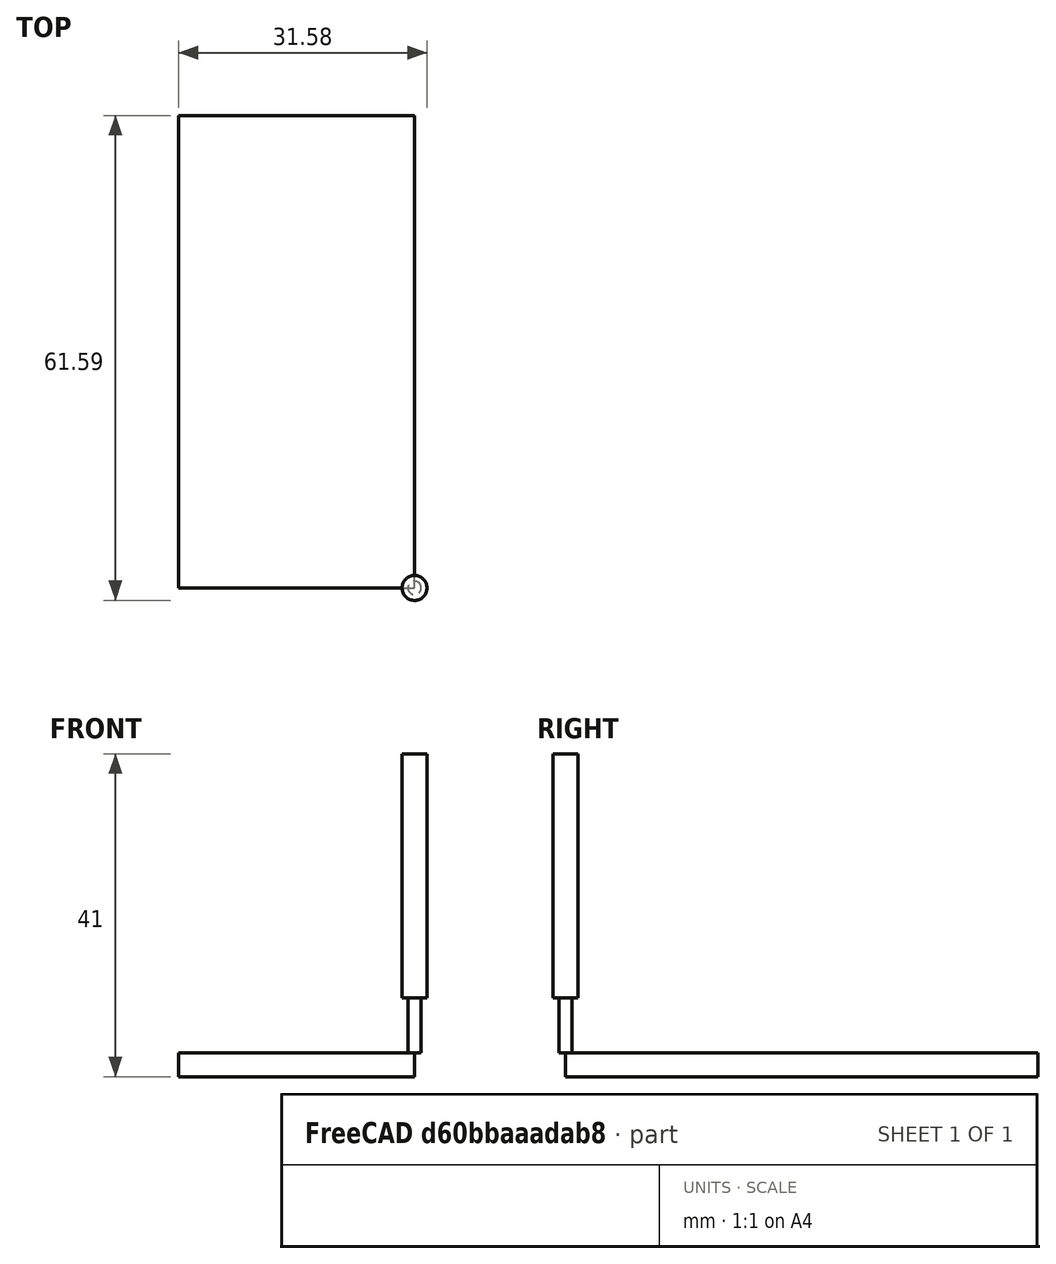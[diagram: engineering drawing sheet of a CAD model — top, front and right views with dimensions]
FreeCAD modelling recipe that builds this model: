
FCSTD DOCUMENT  (FreeCAD 0.20R29603 (Git))
Label: Кріплення дротів (CNC 3018 PLUS)
License: All rights reserved
LicenseURL: http://en.wikipedia.org/wiki/All_rights_reserved
objects: Path::FeaturePython×4, Part::FeaturePython×3, App::DocumentObjectGroup×3, Sketcher::SketchObject×1, PartDesign::Pad×1, PartDesign::Body×1, App::FeaturePython×1, Mesh::FeaturePython×1
note: 9 computed .brp shape members not serialized (recipe doc carries the construction recipe); baked Part::Feature solids carry a one-line shape summary decoded from their .brp

FEATURE [Sketcher::SketchObject] Sketch
  FullyConstrained = true
  MapMode = 5
  Support = -> [XY_Plane]
  sketch-geometry (10):
    g0: LineSegment StartX=-30 StartY=60 StartZ=0 EndX=0 EndY=60 EndZ=0
    g1: LineSegment StartX=0 StartY=60 StartZ=0 EndX=0 EndY=0 EndZ=0
    g2: LineSegment StartX=0 StartY=0 StartZ=0 EndX=-30 EndY=0 EndZ=0
    g3: LineSegment StartX=-30 StartY=0 StartZ=0 EndX=-30 EndY=60 EndZ=0
    g4: Circle CenterX=-22.5 CenterY=5 CenterZ=0 NormalX=0 NormalY=0 NormalZ=1 AngleXU=0 Radius=2.5
    g5: Circle CenterX=-7.5 CenterY=5 CenterZ=0 NormalX=0 NormalY=0 NormalZ=1 AngleXU=0 Radius=2.5
    g6: Circle CenterX=-25 CenterY=55 CenterZ=0 NormalX=0 NormalY=0 NormalZ=1 AngleXU=0 Radius=2
    g7: Circle CenterX=-5 CenterY=55 CenterZ=0 NormalX=0 NormalY=0 NormalZ=1 AngleXU=0 Radius=2
    g8: Circle CenterX=-25 CenterY=30 CenterZ=0 NormalX=0 NormalY=0 NormalZ=1 AngleXU=0 Radius=2
    g9: Circle CenterX=-5 CenterY=30 CenterZ=0 NormalX=0 NormalY=0 NormalZ=1 AngleXU=0 Radius=2
  constraints (29):
    c: Coincident(g0,g1)
    c: Coincident(g1,g2)
    c: Coincident(g2,g3)
    c: Coincident(g3,g0)
    c: Horizontal(g0)
    c: Horizontal(g2)
    c: Vertical(g1)
    c: Vertical(g3)
    c: Coincident(g1,g-1)
    c: DistanceY(g3,g3) = 60
    c: DistanceX(g0,g0) = 30
    c: Distance(g4,g2) = 5
    c: Distance(g5,g2) = 5
    c: Distance(g4,g5) = 15
    c: Diameter(g4) = 5
    c: Diameter(g5) = 5
    c: Distance(g4,g3) = 7.5
    c: Diameter(g6) = 4
    c: Diameter(g7) = 4
    c: Distance(g6,g0) = 5
    c: Distance(g7,g0) = 5
    c: Distance(g6,g3) = 5
    c: Distance(g7,g1) = 5
    c: Diameter(g9) = 4
    c: Diameter(g8) = 4
    c: Distance(g8,g3) = 5
    c: Distance(g9,g1) = 5
    c: Distance(g6,g8) = 25
    c: Distance(g7,g9) = 25
FEATURE [PartDesign::Pad] Pad
  Direction = (0,0,1)
  Length = 3
  Length2 = 10
  Profile = -> Sketch
  ReferenceAxis = -> Sketch [N_Axis]
  Reversed = true
  Type = 0
FEATURE [PartDesign::Body] Body
  Group = -> [Sketch,Pad]
  Origin = -> Origin
  Tip = -> Pad
FEATURE [App::FeaturePython] SetupSheet  # Path/CAM operation (typed FeaturePython)
  ClearanceHeightExpression = OpStockZMax+SetupSheet.ClearanceHeightOffset
  ClearanceHeightOffset = 5
  CoolantMode = 0
  CoolantModes = None | Flood | Mist
  FinalDepthExpression = OpFinalDepth
  HorizRapid = 0
  SafeHeightExpression = OpStockZMax+SetupSheet.SafeHeightOffset
  SafeHeightOffset = 3
  StartDepthExpression = OpStartDepth
  StepDownExpression = OpToolDiameter
  VertRapid = 0
FEATURE [Part::FeaturePython] Clone  label="Model-Body"  # Draft clone (typed FeaturePython)
  AttacherType = Attacher::AttachEngine3D
  Fuse = false
  Objects = -> [Body]
  PathResource = Model
  Scale = (1,1,1)
FEATURE [App::DocumentObjectGroup] Model
  Group = -> [Clone]
FEATURE [Part::FeaturePython] Stock001  # WARN: FeaturePython — macro-defined, semantics opaque (R4)
  Height = 3
  Length = 30
  Placement = pos=(-30,0,-3) rot=(0,0,1;0rad)
  StockType = CreateBox
  Width = 60
FEATURE [Part::FeaturePython] ToolBit001  label="kukuruza-1.7-7-3.175"  # Path/CAM toolbit (typed FeaturePython)
  BitPropertyNames = Chipload | CuttingEdgeHeight | Diameter | Flutes | Length | Material | ShankDiameter | SpindleDirection
  BitShape = <path>
  Chipload = 0
  CuttingEdgeHeight = 7
  Diameter = 1.7
  File = <userpath>/FreeCAD/toolbits/Bit/kukuruza-1.7-7-3.fctb
  Flutes = 0
  Length = 38
  Material = 0
  ShankDiameter = 3.17
  ShapeName = endmill
  SpindleDirection = 0
FEATURE [Path::FeaturePython] kukuruza_1_7_7_3_175  label="kukuruza-1.7-7-3.176"  # Path/CAM operation (typed FeaturePython)
  HorizFeed = 200
  HorizRapid = 200
  SpindleDir = 0
  SpindleSpeed = 1000
  Tool = -> ToolBit001
  ToolNumber = 2
  VertFeed = 200
  VertRapid = 200
  expr: HorizFeed = 200
  expr: HorizRapid = 200
  expr: VertRapid = 200
FEATURE [App::DocumentObjectGroup] Tools
  Group = -> [kukuruza_1_7_7_3_175]
FEATURE [Path::FeaturePython] Profile  label="Отверстия"  # Path/CAM operation (typed FeaturePython)
  Active = true
  AreaParams:
    Tolerance = 1e-07
    FitArcs = True
    Simplify = False
    CleanDistance = 0.0
    Accuracy = 0.01
    Unit = 1.0
    MinArcPoints = 4
    MaxArcPoints = 100
    ClipperScale = 10000000.0
    Fill = 0
    Coplanar = 0
    Reorient = True
    Outline = False
    Explode = False
    OpenMode = 0
    Deflection = 0.01
    SubjectFill = 0
    ClipFill = 0
    Offset = -0.85
    ExtraPass = 0
    Stepover = 0.0
    LastStepover = 0.0
    JoinType = 0
    EndType = 0
    MiterLimit = 2.0
    RoundPrecision = 0.0
    PocketMode = 0
    ToolRadius = 1.0
    PocketExtraOffset = 0.0
    PocketStepover = 0.0
    PocketLastStepover = 0.0
    FromCenter = False
    Angle = 45.0
    AngleShift = 0.0
    Shift = 0.0
    Thicken = False
    SectionCount = -1
    Stepdown = 1.0
    SectionOffset = 0.0
    SectionTolerance = 1e-06
    SectionMode = 2
    Project = False
  Base = -> [Clone]
  ClearanceHeight = 5
  CoolantMode = 0
  CycleTime = 00:00:06
  Direction = 0
  FinalDepth = -3
  HandleMultipleFeatures = 0
  JoinType = 0
  MiterLimit = 0.1
  OffsetExtra = 0
  OpFinalDepth = -3
  OpStartDepth = 0
  OpStockZMax = 0
  OpStockZMin = -3
  OpToolDiameter = 1.7
  PathParams = {'orientation': 1, 'feedrate': 200.0, 'feedrate_v': 200.0, 'verbose': True, 'resume_height': 3.0, 'retraction': 5.0, 'return_end': True, 'preamble': False}
  SafeHeight = 3
  Side = 1
  SplitArcs = false
  StartDepth = 0
  StartPoint = (0,0,0)
  StepDown = 0.5
  ToolController = -> kukuruza_1_7_7_3_175
  UseComp = true
  UseStartPoint = false
  processCircles = false
  processHoles = false
  processPerimeter = true
  expr: ClearanceHeight = OpStockZMax + SetupSheet.ClearanceHeightOffset
  expr: FinalDepth = OpFinalDepth
  expr: SafeHeight = OpStockZMax + SetupSheet.SafeHeightOffset
  expr: StartDepth = OpStartDepth
  expr: StepDown = 0.5
FEATURE [Path::FeaturePython] Profile001  label="Контур"  # Path/CAM operation (typed FeaturePython)
  Active = true
  AreaParams:
    Tolerance = 1e-07
    FitArcs = True
    Simplify = False
    CleanDistance = 0.0
    Accuracy = 0.01
    Unit = 1.0
    MinArcPoints = 4
    MaxArcPoints = 100
    ClipperScale = 10000000.0
    Fill = 0
    Coplanar = 0
    Reorient = True
    Outline = False
    Explode = False
    OpenMode = 0
    Deflection = 0.01
    SubjectFill = 0
    ClipFill = 0
    Offset = 0.85
    ExtraPass = 0
    Stepover = 0.0
    LastStepover = 0.0
    JoinType = 0
    EndType = 0
    MiterLimit = 2.0
    RoundPrecision = 0.0
    PocketMode = 0
    ToolRadius = 1.0
    PocketExtraOffset = 0.0
    PocketStepover = 0.0
    PocketLastStepover = 0.0
    FromCenter = False
    Angle = 45.0
    AngleShift = 0.0
    Shift = 0.0
    Thicken = False
    SectionCount = -1
    Stepdown = 1.0
    SectionOffset = 0.0
    SectionTolerance = 1e-06
    SectionMode = 2
    Project = False
  Base = -> [Clone]
  ClearanceHeight = 5
  CoolantMode = 0
  CycleTime = 00:00:05
  Direction = 0
  FinalDepth = -3
  HandleMultipleFeatures = 0
  JoinType = 0
  MiterLimit = 0.1
  OffsetExtra = 0
  OpFinalDepth = -3
  OpStartDepth = 0
  OpStockZMax = 0
  OpStockZMin = -3
  OpToolDiameter = 1.7
  PathParams = {'orientation': 1, 'feedrate': 200.0, 'feedrate_v': 200.0, 'verbose': True, 'resume_height': 3.0, 'retraction': 5.0, 'return_end': True, 'preamble': False}
  SafeHeight = 3
  Side = 0
  SplitArcs = false
  StartDepth = 0
  StartPoint = (0,0,0)
  StepDown = 0.5
  ToolController = -> kukuruza_1_7_7_3_175
  UseComp = true
  UseStartPoint = false
  processCircles = false
  processHoles = false
  processPerimeter = true
  expr: ClearanceHeight = OpStockZMax + SetupSheet.ClearanceHeightOffset
  expr: FinalDepth = OpFinalDepth
  expr: SafeHeight = OpStockZMax + SetupSheet.SafeHeightOffset
  expr: StartDepth = OpStartDepth
  expr: StepDown = 0.5
FEATURE [App::DocumentObjectGroup] Operations
  Group = -> [Profile,Profile001]
FEATURE [Path::FeaturePython] Job  # Path/CAM operation (typed FeaturePython)
  CycleTime = 00:00:11
  Fixtures = G59
  GeometryTolerance = 0.01
  JobType = 0
  LastPostProcessDate = 2023-05-25 23:59:38.165799
  LastPostProcessOutput = <userpath>/Gcode/1.ngc
  Model = -> Model
  Operations = -> Operations
  OrderOutputBy = 0
  PostProcessor = 11
  SetupSheet = -> SetupSheet
  SplitOutput = false
  Stock = -> Stock001
  Tools = -> Tools
FEATURE [Mesh::FeaturePython] CutMaterial  # WARN: FeaturePython — macro-defined, semantics opaque (R4)
note: 1 file-system path scrubbed to <path> (originals preserved in the JSON sidecar)
